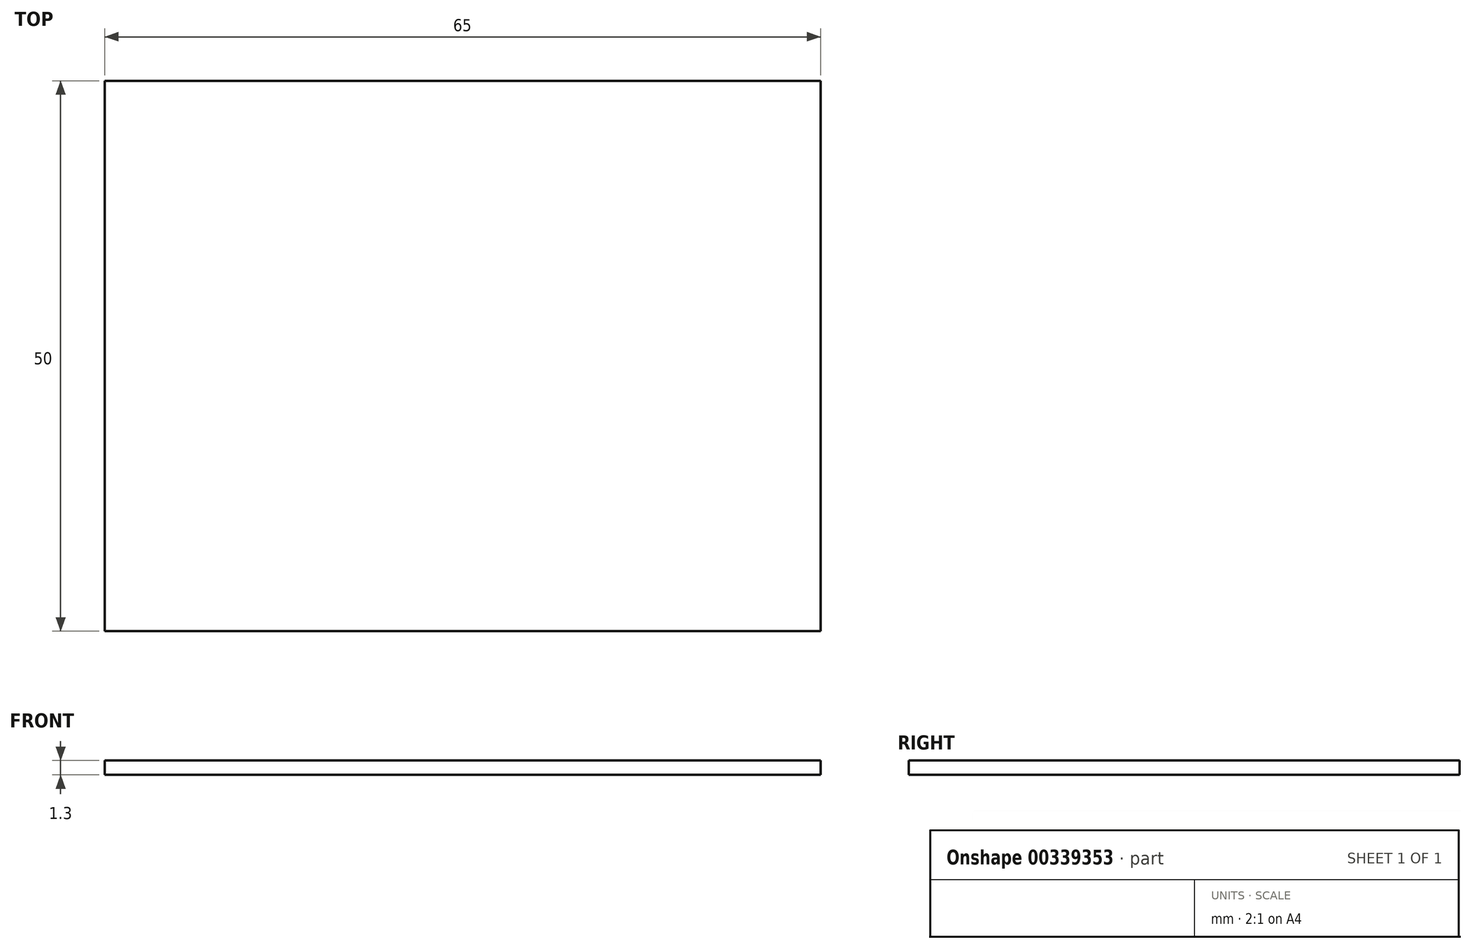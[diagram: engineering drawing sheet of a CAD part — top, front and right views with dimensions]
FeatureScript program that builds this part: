
annotation { "Feature Type Name" : "Feature", "Feature Type Description" : "" }
export const myFeature = defineFeature(function(context is Context, id is Id, definition is map)
    precondition{}
    {
        {
            var Q0;
            Q0=qCreatedBy(makeId("Top.planeOp"),FACE);
            var sketch = newSketch(context, id + "F0", { "sketchPlane" : qUnion([Q0])});
            skLineSegment(sketch, "E0", {"start": v(0, 0) * mm, "end": v(-65, 0) * mm});
            skLineSegment(sketch, "E1", {"start": v(0, 0) * mm, "end": v(0, 50) * mm});
            skLineSegment(sketch, "E2", {"start": v(0, 50) * mm, "end": v(-65, 50) * mm});
            skLineSegment(sketch, "E3", {"start": v(-65, 50) * mm, "end": v(-65, 0) * mm});
            skSolve(sketch);
        }
        {
            var Q0;
            Q0 = qSketchRegion(id + "F0", true);
            extrude(context, id + "F1", {"entities" : qUnion([Q0]), "depth" : 1.3 * mm});
        }
    });
